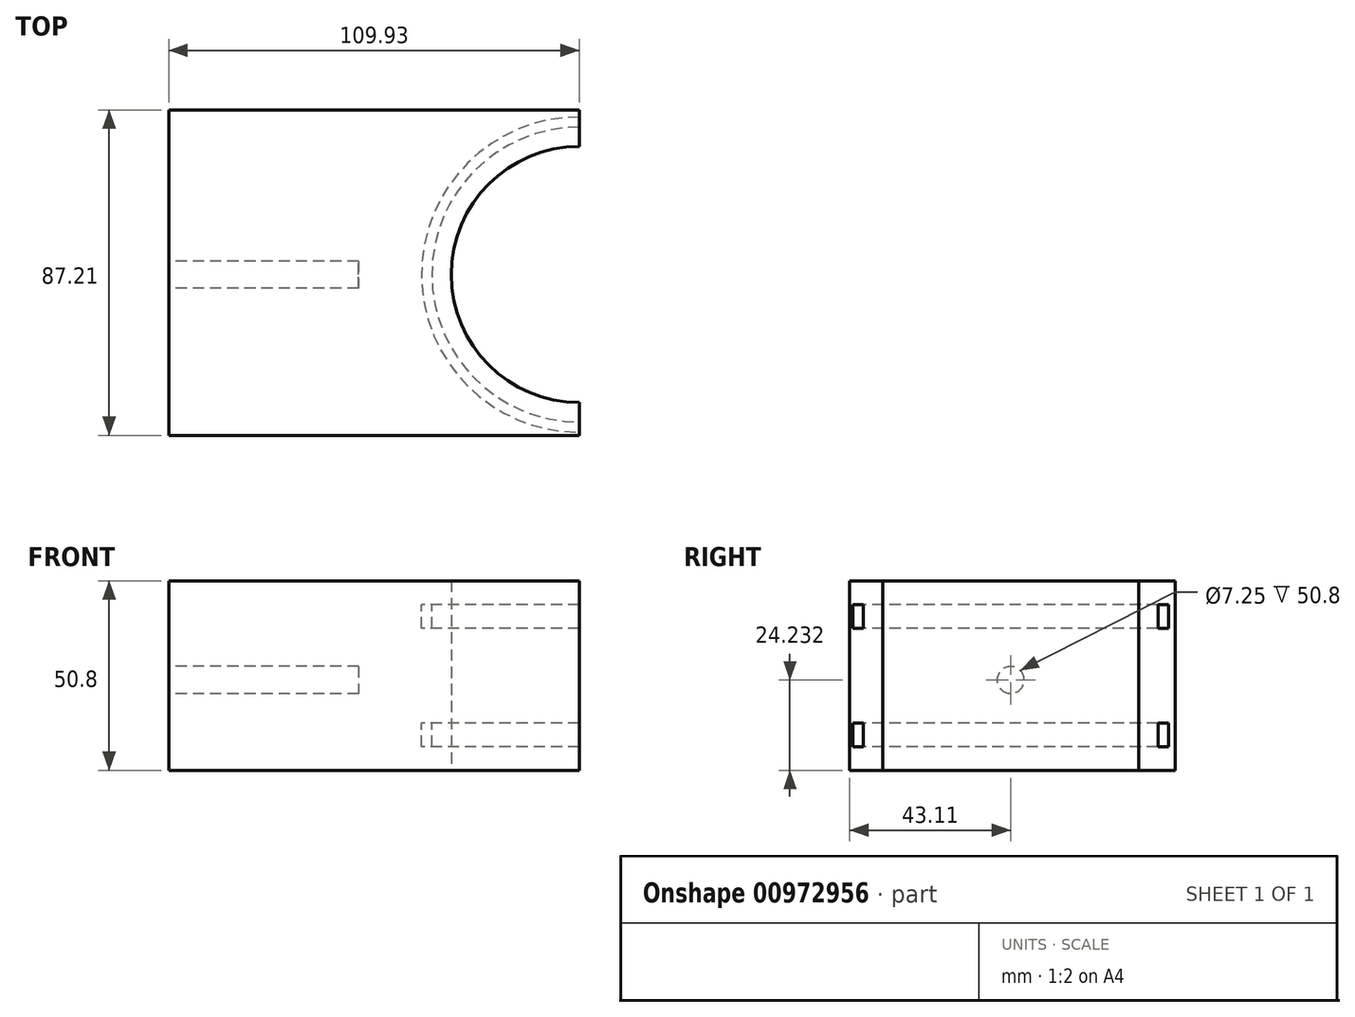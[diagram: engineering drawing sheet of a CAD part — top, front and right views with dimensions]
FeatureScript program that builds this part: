
annotation { "Feature Type Name" : "Feature", "Feature Type Description" : "" }
export const myFeature = defineFeature(function(context is Context, id is Id, definition is map)
    precondition{}
    {
        {
            var Q0;
            Q0=qCreatedBy(makeId("Top.planeOp"),FACE);
            var sketch = newSketch(context, id + "F0", { "sketchPlane" : qUnion([Q0])});
            skLineSegment(sketch, "E0.bottom", {"start": v(-50.84, 44.1) * mm, "end": v(59.1, 44.1) * mm});
            skLineSegment(sketch, "E0.top", {"start": v(-50.84, -43.11) * mm, "end": v(59.1, -43.11) * mm});
            skLineSegment(sketch, "E0.left", {"start": v(-50.84, 44.1) * mm, "end": v(-50.84, -43.11) * mm});
            skLineSegment(sketch, "E0.right", {"start": v(59.1, 44.1) * mm, "end": v(59.1, 34.32) * mm});
            skArc(sketch, "E1", {"start": v(59.1, 34.32) * mm, "mid": v(24.77, 0) * mm, "end": v(59.1, -34.32) * mm});
            skLineSegment(sketch, "E2.trimOffspring", {"start": v(59.1, -34.32) * mm, "end": v(59.1, -43.11) * mm});
            skSolve(sketch);
        }
        {
            var Q0;
            Q0 = qSketchRegion(id + "F0", true);
            extrude(context, id + "F1", {"entities" : qUnion([Q0]), "depth" : 50.8 * mm, "offsetDistance" : 25.4 * mm});
        }
        {
            var Q0;
            Q0=makeQuery(id+"F1.opExtrude","SWEPT_FACE",FACE,{"disambiguationData":[OSD([sQuery(id+"F0.wireOp",EDGE,"E0.left")])]});
            var sketch = newSketch(context, id + "F2", { "sketchPlane" : qUnion([Q0])});
            skCircle(sketch, "E3", {"center": v(0, 24.23) * mm, "radius": 3.63 * mm});
            skSolve(sketch);
        }
        {
            var Q0;
            Q0=makeQuery(id+"F2.imprint","IMPRINT",FACE,{"disambiguationData":[TD([[makeQuery(id+"F2.imprint","IMPRINT",EDGE,{"derivedFrom":sQuery(id+"F2.wireOp",EDGE,"E3")}),1.0]])]});
            extrude(context, id + "F3", {"entities" : qUnion([Q0]), "operationType" : NewBodyOperationType.REMOVE, "oppositeDirection" : true, "depth" : 50.8 * mm, "offsetDistance" : 25.4 * mm});
        }
        {
            var Q0;
            Q0=makeQuery(id+"F1.opExtrude","CAP_FACE",FACE,{"disambiguationData":[OSD([sQuery(id+"F0.wireOp",EDGE,"E0.bottom"),sQuery(id+"F0.wireOp",EDGE,"E0.top"),sQuery(id+"F0.wireOp",EDGE,"E0.left"),sQuery(id+"F0.wireOp",EDGE,"E0.right"),sQuery(id+"F0.wireOp",EDGE,"E1"),sQuery(id+"F0.wireOp",EDGE,"E2.trimOffspring")])],"isStart":false});
            var sketch = newSketch(context, id + "F4", { "sketchPlane" : qUnion([Q0])});
            skArc(sketch, "E4", {"start": v(59.1, 39.5) * mm, "mid": v(19.58, 0) * mm, "end": v(59.1, -39.5) * mm});
            skArc(sketch, "E5", {"start": v(59.1, 42.26) * mm, "mid": v(16.84, 0) * mm, "end": v(59.1, -42.26) * mm});
            skLineSegment(sketch, "E6", {"start": v(59.1, 39.2) * mm, "end": v(59.1, 42.26) * mm});
            skLineSegment(sketch, "E7", {"start": v(59.1, 42.26) * mm, "end": v(59.1, 39.2) * mm});
            skLineSegment(sketch, "E8.trimOffspring", {"start": v(59.1, -39.5) * mm, "end": v(59.1, -42.26) * mm});
            skSolve(sketch);
        }
        {
            var Q0;
            {var subQ0=sQuery(id+"F4.wireOp",EDGE,"E4");Q0=makeQuery(id+"F4.imprint","IMPRINT",FACE,{"disambiguationData":[TD([[makeQuery(id+"F4.imprint","IMPRINT",EDGE,{"derivedFrom":subQ0}),-1.0]])]});}
            var Q1;
            Q1=sQuery(id+"F4.wireOp",EDGE,"E5");
            var Q2;
            Q2=sQuery(id+"F4.wireOp",EDGE,"E4");
            extrude(context, id + "F5", {"entities" : qUnion([Q0]), "operationType" : NewBodyOperationType.REMOVE, "surfaceEntities" : qUnion([Q1, Q2]), "oppositeDirection" : true, "depth" : 44.45 * mm, "offsetDistance" : 25.4 * mm});
        }
        {
            var Q0;
            {var subQ0=sQuery(id+"F4.wireOp",EDGE,"E4");Q0=makeQuery(id+"F4.imprint","IMPRINT",FACE,{"disambiguationData":[TD([[makeQuery(id+"F4.imprint","IMPRINT",EDGE,{"derivedFrom":subQ0}),-1.0]])]});}
            extrude(context, id + "F6", {"entities" : qUnion([Q0]), "operationType" : NewBodyOperationType.ADD, "oppositeDirection" : true, "depth" : 38.1 * mm, "offsetDistance" : 25.4 * mm});
        }
        {
            var Q0;
            {var subQ0=sQuery(id+"F4.wireOp",EDGE,"E4");Q0=makeQuery(id+"F4.imprint","IMPRINT",FACE,{"disambiguationData":[TD([[makeQuery(id+"F4.imprint","IMPRINT",EDGE,{"derivedFrom":subQ0}),-1.0]])]});}
            extrude(context, id + "F7", {"entities" : qUnion([Q0]), "operationType" : NewBodyOperationType.REMOVE, "oppositeDirection" : true, "depth" : 12.7 * mm, "offsetDistance" : 25.4 * mm});
        }
        {
            var Q0;
            {var subQ0=sQuery(id+"F4.wireOp",EDGE,"E4");Q0=makeQuery(id+"F4.imprint","IMPRINT",FACE,{"disambiguationData":[TD([[makeQuery(id+"F4.imprint","IMPRINT",EDGE,{"derivedFrom":subQ0}),-1.0]])]});}
            var Q1;
            Q1=sQuery(id+"F4.wireOp",EDGE,"E5");
            var Q2;
            Q2=sQuery(id+"F4.wireOp",EDGE,"E4");
            extrude(context, id + "F8", {"entities" : qUnion([Q0]), "operationType" : NewBodyOperationType.ADD, "surfaceEntities" : qUnion([Q1, Q2]), "oppositeDirection" : true, "depth" : 6.35 * mm, "offsetDistance" : 25.4 * mm});
        }
    });
